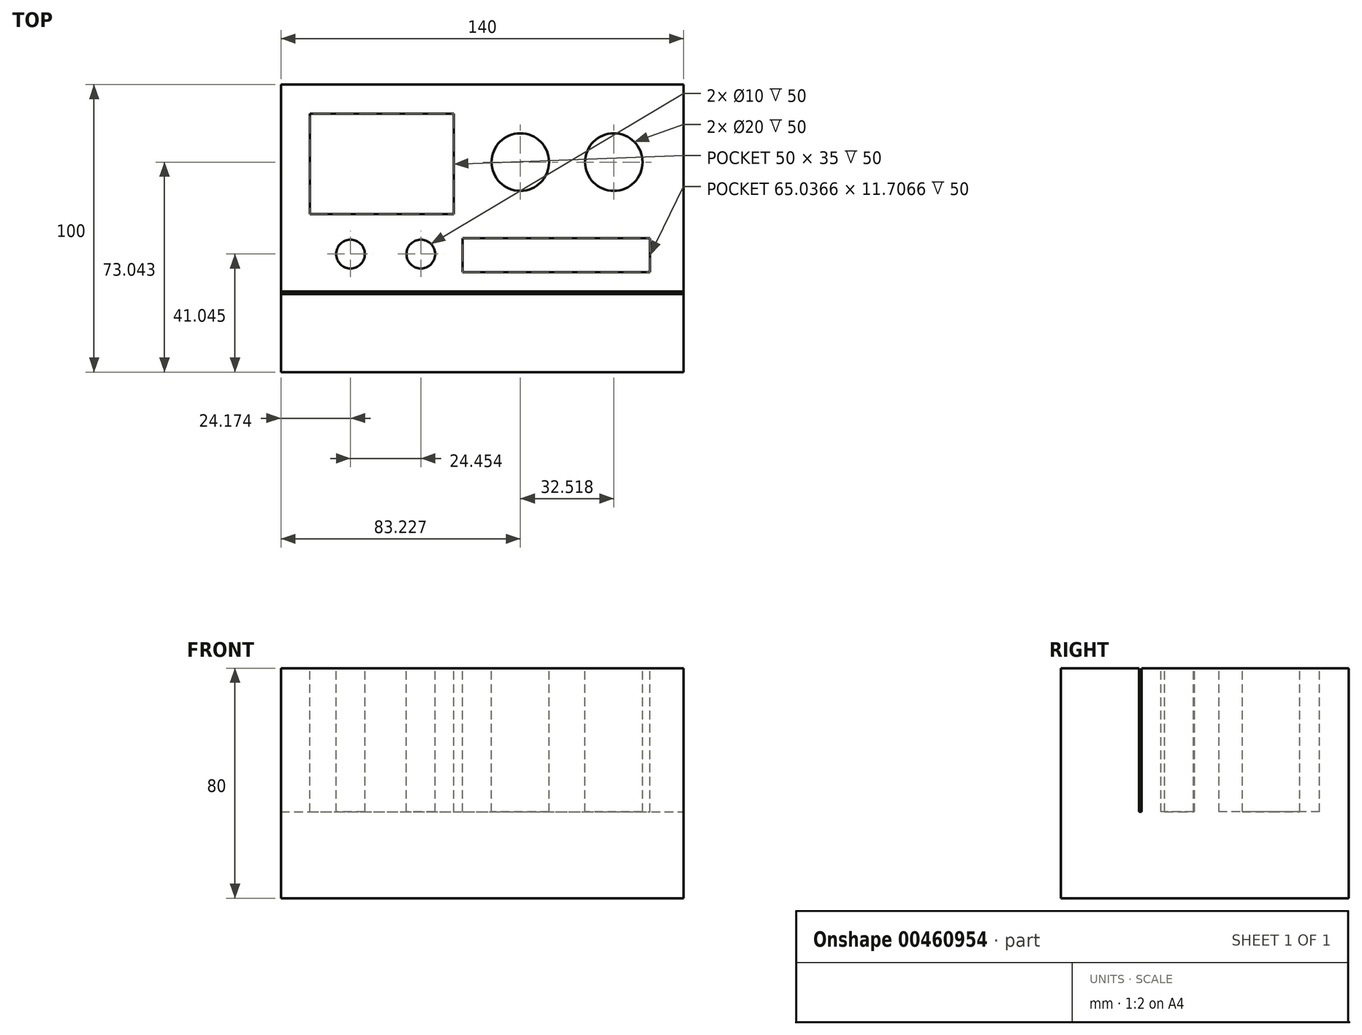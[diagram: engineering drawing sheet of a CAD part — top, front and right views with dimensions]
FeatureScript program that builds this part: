
annotation { "Feature Type Name" : "Feature", "Feature Type Description" : "" }
export const myFeature = defineFeature(function(context is Context, id is Id, definition is map)
    precondition{}
    {
        {
            var Q0;
            Q0=qCreatedBy(makeId("Top.planeOp"),FACE);
            var sketch = newSketch(context, id + "F0", { "sketchPlane" : qUnion([Q0])});
            skLineSegment(sketch, "E0.bottom", {"start": v(-31.61, 85.61) * mm, "end": v(108.39, 85.61) * mm});
            skLineSegment(sketch, "E0.top", {"start": v(-31.61, -14.39) * mm, "end": v(108.39, -14.39) * mm});
            skLineSegment(sketch, "E0.left", {"start": v(-31.61, 85.61) * mm, "end": v(-31.61, -14.39) * mm});
            skLineSegment(sketch, "E0.right", {"start": v(108.39, 85.61) * mm, "end": v(108.39, -14.39) * mm});
            skSolve(sketch);
        }
        {
            var Q0;
            Q0=makeQuery(id+"F0.imprint","IMPRINT",FACE,{"disambiguationData":[TD([[makeQuery(id+"F0.imprint","IMPRINT",EDGE,{"derivedFrom":sQuery(id+"F0.wireOp",EDGE,"E0.bottom")}),-1.0]])]});
            extrude(context, id + "F1", {"entities" : qUnion([Q0]), "depth" : 80 * mm, "offsetDistance" : 25 * mm});
        }
        {
            var Q0;
            Q0=makeQuery(id+"F1.opExtrude","CAP_FACE",FACE,{"disambiguationData":[OSD([sQuery(id+"F0.wireOp",EDGE,"E0.bottom"),sQuery(id+"F0.wireOp",EDGE,"E0.top"),sQuery(id+"F0.wireOp",EDGE,"E0.left"),sQuery(id+"F0.wireOp",EDGE,"E0.right")])],"isStart":false});
            var sketch = newSketch(context, id + "F2", { "sketchPlane" : qUnion([Q0])});
            skPoint(sketch, "E1", {"position": v(-31.61, 5.61) * mm});
            skPoint(sketch, "E2", {"position": v(-31.61, -14.39) * mm});
            skPoint(sketch, "E3", {"position": v(108.39, -14.39) * mm});
            skPoint(sketch, "E4", {"position": v(108.14, 85.57) * mm});
            skPoint(sketch, "E5", {"position": v(-31.61, 85.61) * mm});
            skLineSegment(sketch, "E6.bottom", {"start": v(-31.61, 13.62) * mm, "end": v(108.39, 13.62) * mm});
            skLineSegment(sketch, "E6.top", {"start": v(-31.61, 12.8) * mm, "end": v(108.39, 12.8) * mm});
            skLineSegment(sketch, "E6.left", {"start": v(-31.61, 13.62) * mm, "end": v(-31.61, 12.8) * mm});
            skLineSegment(sketch, "E6.right", {"start": v(108.39, 13.62) * mm, "end": v(108.39, 12.8) * mm});
            skPoint(sketch, "E7", {"position": v(-31.61, 66.52) * mm});
            skPoint(sketch, "E8", {"position": v(-13.91, 85.61) * mm});
            skLineSegment(sketch, "E9.bottom", {"start": v(-31.5, 85.52) * mm, "end": v(-21.5, 85.52) * mm});
            skLineSegment(sketch, "E9.left", {"start": v(-31.5, 85.52) * mm, "end": v(-31.5, 75.52) * mm});
            skLineSegment(sketch, "E10.bottom", {"start": v(108.14, 85.57) * mm, "end": v(98.14, 85.57) * mm});
            skLineSegment(sketch, "E10.left", {"start": v(108.14, 85.57) * mm, "end": v(108.14, 75.57) * mm});
            skLineSegment(sketch, "E11.bottom", {"start": v(-21.5, 75.52) * mm, "end": v(28.5, 75.52) * mm});
            skLineSegment(sketch, "E11.top", {"start": v(-21.5, 40.52) * mm, "end": v(28.5, 40.52) * mm});
            skLineSegment(sketch, "E11.left", {"start": v(-21.5, 75.52) * mm, "end": v(-21.5, 40.52) * mm});
            skLineSegment(sketch, "E11.right", {"start": v(28.5, 75.52) * mm, "end": v(28.5, 40.52) * mm});
            skCircle(sketch, "E12", {"center": v(51.62, 58.65) * mm, "radius": 10 * mm});
            skCircle(sketch, "E13", {"center": v(84.14, 58.65) * mm, "radius": 10 * mm});
            skCircle(sketch, "E14", {"center": v(-7.44, 26.66) * mm, "radius": 5 * mm});
            skCircle(sketch, "E15", {"center": v(17.02, 26.66) * mm, "radius": 5 * mm});
            skPoint(sketch, "E16.center.orphan", {"position": v(38.39, 26.66) * mm});
            skLineSegment(sketch, "E17.bottom", {"start": v(31.59, 32.12) * mm, "end": v(96.62, 32.12) * mm});
            skLineSegment(sketch, "E17.top", {"start": v(31.59, 20.41) * mm, "end": v(96.62, 20.41) * mm});
            skLineSegment(sketch, "E17.left", {"start": v(31.59, 32.12) * mm, "end": v(31.59, 20.41) * mm});
            skLineSegment(sketch, "E17.right", {"start": v(96.62, 32.12) * mm, "end": v(96.62, 20.41) * mm});
            skPoint(sketch, "E18.orphan", {"position": v(-31.61, 26.66) * mm});
            skPoint(sketch, "E19.trimOffspring.end.orphan", {"position": v(108.39, 26.66) * mm});
            skSolve(sketch);
        }
        {
            var Q0;
            Q0=sQuery(id+"F2.wireOp",EDGE,"E6.bottom");
            extrude(context, id + "F3", {"bodyType" : ToolBodyType.SURFACE, "surfaceEntities" : qUnion([Q0]), "depth" : -5 * mm, "offsetDistance" : 25 * mm});
        }
        {
            var Q0;
            Q0 = qSketchRegion(id + "F2", true);
            extrude(context, id + "F4", {"entities" : qUnion([Q0]), "operationType" : NewBodyOperationType.REMOVE, "depth" : -50 * mm});
        }
        {
            var Q0;
            Q0=makeQuery(id+"F1.opExtrude","SWEPT_FACE",FACE,{"disambiguationData":[OSD([sQuery(id+"F0.wireOp",EDGE,"E0.top")])]});
            var sketch = newSketch(context, id + "F5", { "sketchPlane" : qUnion([Q0])});
            skText(sketch, "E20", { "text": "ADMINISTRATIVO\n    IES RODEIRA", "fontName": "OpenSans-Bold.ttf"});
            const initialGuessF5  = {"E20": [-0.02244, 0.04593, 1, 0, 0.0105]};
            skSetInitialGuess(sketch, initialGuessF5);
            skSolve(sketch);
        }
        {
            var Q0;
            Q0 = qSketchRegion(id + "F5", true);
            extrude(context, id + "F6", {"entities" : qUnion([Q0]), "operationType" : NewBodyOperationType.ADD, "depth" : -15 * mm});
        }
    });
